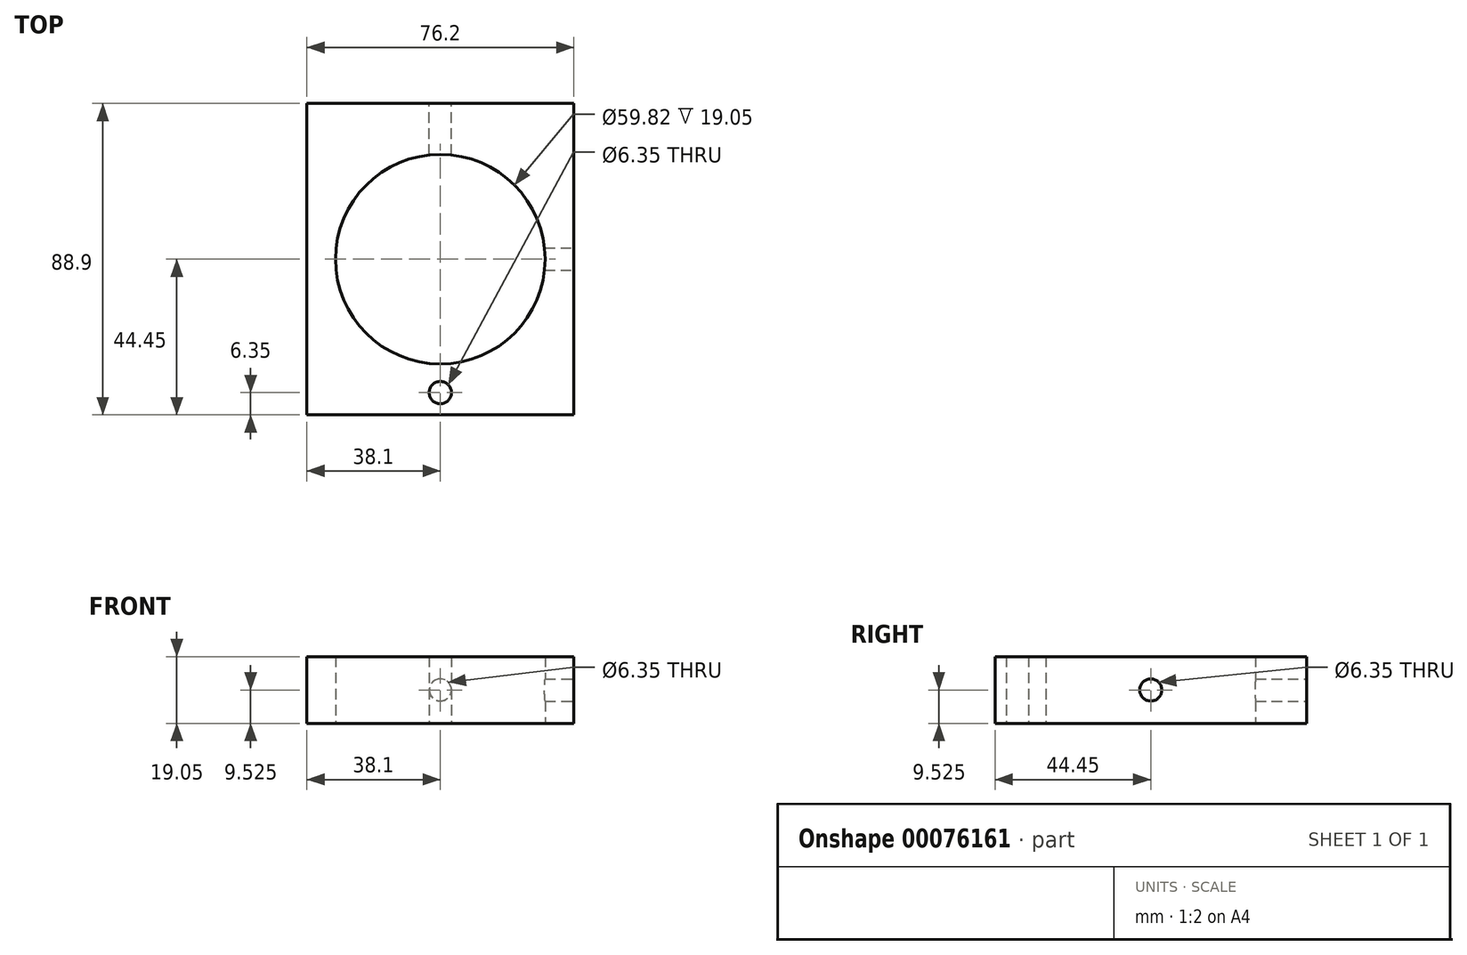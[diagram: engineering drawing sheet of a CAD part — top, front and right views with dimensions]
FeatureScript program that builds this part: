
annotation { "Feature Type Name" : "Feature", "Feature Type Description" : "" }
export const myFeature = defineFeature(function(context is Context, id is Id, definition is map)
    precondition{}
    {
        {
            var Q0;
            Q0=qCreatedBy(makeId("Top.planeOp"),FACE);
            var sketch = newSketch(context, id + "F0", { "sketchPlane" : qUnion([Q0])});
            skLineSegment(sketch, "E0.bottom", {"start": v(38.1, 44.45) * mm, "end": v(-38.1, 44.45) * mm});
            skLineSegment(sketch, "E0.top", {"start": v(38.1, -44.45) * mm, "end": v(-38.1, -44.45) * mm});
            skLineSegment(sketch, "E0.left", {"start": v(38.1, 44.45) * mm, "end": v(38.1, -44.45) * mm});
            skLineSegment(sketch, "E0.right", {"start": v(-38.1, 44.45) * mm, "end": v(-38.1, -44.45) * mm});
            skPoint(sketch, "E0.middle", {"position": v(0, 0) * mm});
            skCircle(sketch, "E1", {"center": v(0, 0) * mm, "radius": 29.9 * mm});
            skCircle(sketch, "E2", {"center": v(0, -38.1) * mm, "radius": 3.18 * mm});
            skSolve(sketch);
        }
        {
            var Q0;
            Q0 = qSketchRegion(id + "F0", true);
            extrude(context, id + "F1", {"entities" : qUnion([Q0]), "depth" : 19.05 * mm});
        }
        {
            var Q0;
            Q0=makeQuery(id+"F1.opExtrude","SWEPT_FACE",FACE,{"disambiguationData":[OSD([sQuery(id+"F0.wireOp",EDGE,"E0.left")])]});
            var sketch = newSketch(context, id + "F2", { "sketchPlane" : qUnion([Q0])});
            skCircle(sketch, "E3", {"center": v(0, 9.53) * mm, "radius": 3.18 * mm});
            skPoint(sketch, "E3.centerSnap0", {"position": v(44.45, 9.53) * mm});
            skPoint(sketch, "E3.centerSnap1", {"position": v(0, 19.05) * mm});
            skSolve(sketch);
        }
        {
            var Q0;
            Q0 = qSketchRegion(id + "F2", true);
            extrude(context, id + "F3", {"entities" : qUnion([Q0]), "operationType" : NewBodyOperationType.REMOVE, "oppositeDirection" : true, "depth" : 25.4 * mm});
        }
        {
            var Q0;
            Q0=makeQuery(id+"F1.opExtrude","SWEPT_FACE",FACE,{"disambiguationData":[OSD([sQuery(id+"F0.wireOp",EDGE,"E0.bottom")])]});
            var sketch = newSketch(context, id + "F4", { "sketchPlane" : qUnion([Q0])});
            skCircle(sketch, "E4", {"center": v(0, 9.53) * mm, "radius": 3.18 * mm});
            skPoint(sketch, "E4.centerSnap0", {"position": v(38.1, 9.53) * mm});
            skSolve(sketch);
        }
        {
            var Q0;
            Q0 = qSketchRegion(id + "F4", true);
            extrude(context, id + "F5", {"entities" : qUnion([Q0]), "operationType" : NewBodyOperationType.REMOVE, "oppositeDirection" : true, "depth" : 25.4 * mm});
        }
    });
